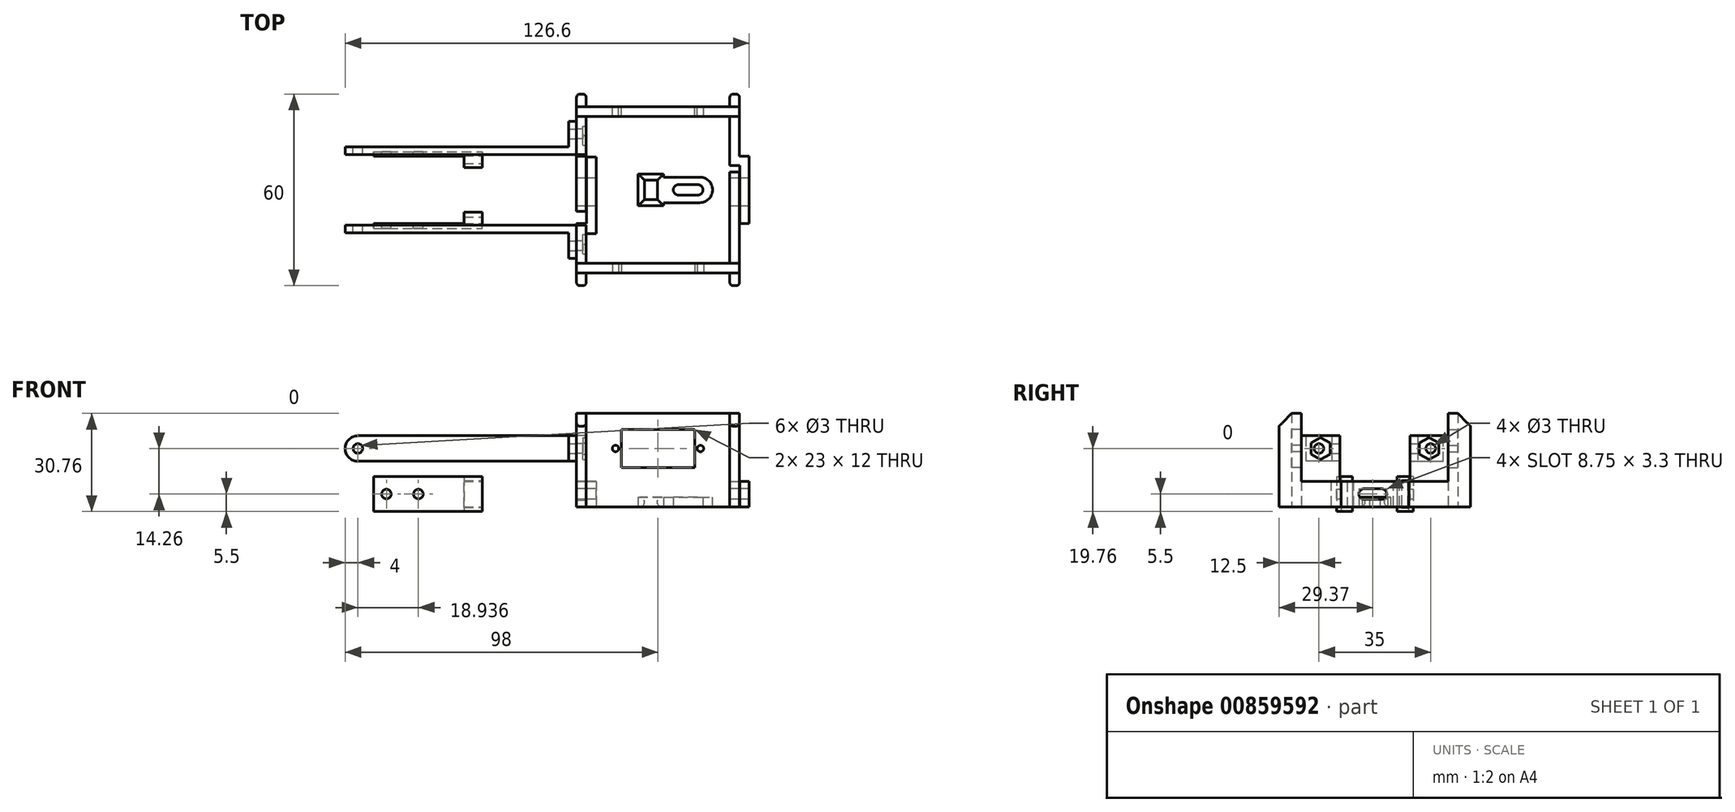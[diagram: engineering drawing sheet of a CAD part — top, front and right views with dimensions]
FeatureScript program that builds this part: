
annotation { "Feature Type Name" : "Feature", "Feature Type Description" : "" }
export const myFeature = defineFeature(function(context is Context, id is Id, definition is map)
    precondition{}
    {
        {
            var Q0;
            Q0=qCreatedBy(makeId("Top.planeOp"),FACE);
            var sketch = newSketch(context, id + "F0", { "sketchPlane" : qUnion([Q0])});
            skLineSegment(sketch, "E0", {"start": v(-48.06, 0) * mm, "end": v(-48.06, 8.5) * mm, "construction": true});
            skLineSegment(sketch, "E1", {"start": v(-48.06, 8.5) * mm, "end": v(-73.06, 8.5) * mm, "construction": true});
            skLineSegment(sketch, "E2", {"start": v(-73.06, 8.5) * mm, "end": v(-73.06, 10.5) * mm, "construction": true});
            skLineSegment(sketch, "E3.MirrorCS", {"start": v(-73.06, -8.5) * mm, "end": v(-73.06, -10.5) * mm, "construction": true});
            skLineSegment(sketch, "E4.MirrorCS", {"start": v(-48.06, -8.5) * mm, "end": v(-73.06, -8.5) * mm, "construction": true});
            skLineSegment(sketch, "E5.MirrorCS", {"start": v(-48.06, 0) * mm, "end": v(-48.06, -8.5) * mm, "construction": true});
            skLineSegment(sketch, "E6.bottom", {"start": v(-22.5, -23) * mm, "end": v(22.5, -23) * mm});
            skLineSegment(sketch, "E6.top", {"start": v(-22.5, 23) * mm, "end": v(22.5, 23) * mm});
            skLineSegment(sketch, "E6.left", {"start": v(-22.5, -23) * mm, "end": v(-22.5, -10.5) * mm});
            skLineSegment(sketch, "E6.right", {"start": v(22.5, -23) * mm, "end": v(22.5, -10.5) * mm});
            skPoint(sketch, "E6.middle", {"position": v(0, 0) * mm});
            skLineSegment(sketch, "E7", {"start": v(-73.06, 10.5) * mm, "end": v(-25.5, 10.5) * mm, "construction": true});
            skLineSegment(sketch, "E8", {"start": v(-25.5, 10.5) * mm, "end": v(-25.5, 26) * mm});
            skLineSegment(sketch, "E9", {"start": v(-25.5, 26) * mm, "end": v(25.5, 26) * mm});
            skLineSegment(sketch, "E10", {"start": v(25.5, 26) * mm, "end": v(25.5, 10.5) * mm});
            skLineSegment(sketch, "E11.MirrorCS", {"start": v(-73.06, -10.5) * mm, "end": v(-25.5, -10.5) * mm, "construction": true});
            skLineSegment(sketch, "E12.MirrorCS", {"start": v(-25.5, -10.5) * mm, "end": v(-25.5, -26) * mm});
            skLineSegment(sketch, "E13.MirrorCS", {"start": v(-25.5, -26) * mm, "end": v(25.5, -26) * mm});
            skLineSegment(sketch, "E14.MirrorCS", {"start": v(25.5, -26) * mm, "end": v(25.5, -10.5) * mm});
            skLineSegment(sketch, "E15", {"start": v(-25.5, 10.5) * mm, "end": v(-25.5, -10.5) * mm, "construction": true});
            skLineSegment(sketch, "E16", {"start": v(-25.5, -10.5) * mm, "end": v(-22.5, -10.5) * mm});
            skLineSegment(sketch, "E17", {"start": v(22.5, -10.5) * mm, "end": v(25.5, -10.5) * mm});
            skLineSegment(sketch, "E18", {"start": v(-25.5, 10.5) * mm, "end": v(-22.5, 10.5) * mm});
            skLineSegment(sketch, "E19", {"start": v(22.5, 10.5) * mm, "end": v(25.5, 10.5) * mm});
            skLineSegment(sketch, "E20.trimOffspring", {"start": v(22.5, 10.5) * mm, "end": v(22.5, 23) * mm});
            skPoint(sketch, "E21.orphan", {"position": v(25.5, 0) * mm});
            skLineSegment(sketch, "E22.trimOffspring", {"start": v(-22.5, 10.5) * mm, "end": v(-22.5, 23) * mm});
            skSolve(sketch);
        }
        {
            var Q0;
            Q0 = qSketchRegion(id + "F0", true);
            extrude(context, id + "F1", {"entities" : qUnion([Q0]), "depth" : 8 * mm, "offsetDistance" : 25 * mm});
        }
        {
            var Q0;
            Q0=makeQuery(id+"F1.opExtrude","SWEPT_FACE",FACE,{"disambiguationData":[OSD([sQuery(id+"F0.wireOp",EDGE,"E13.MirrorCS")])]});
            var sketch = newSketch(context, id + "F2", { "sketchPlane" : qUnion([Q0])});
            skLineSegment(sketch, "E23.bottom", {"start": v(11.5, 12.26) * mm, "end": v(-11.5, 12.26) * mm});
            skLineSegment(sketch, "E23.top", {"start": v(11.5, 24.26) * mm, "end": v(-11.5, 24.26) * mm});
            skLineSegment(sketch, "E23.left", {"start": v(11.5, 12.26) * mm, "end": v(11.5, 24.26) * mm});
            skLineSegment(sketch, "E23.right", {"start": v(-11.5, 12.26) * mm, "end": v(-11.5, 24.26) * mm});
            skLineSegment(sketch, "E24.bottom", {"start": v(25.5, 8) * mm, "end": v(0, 8) * mm});
            skLineSegment(sketch, "E24.top", {"start": v(25.5, 29.26) * mm, "end": v(-25.5, 29.26) * mm});
            skLineSegment(sketch, "E24.left", {"start": v(25.5, 8) * mm, "end": v(25.5, 29.26) * mm});
            skLineSegment(sketch, "E24.right", {"start": v(-25.5, 8) * mm, "end": v(-25.5, 29.26) * mm});
            skCircle(sketch, "E25", {"center": v(13.3, 18.26) * mm, "radius": 1 * mm});
            skPoint(sketch, "E25.centerSnap0", {"position": v(11.5, 18.26) * mm});
            skCircle(sketch, "E26", {"center": v(-13.3, 18.26) * mm, "radius": 1 * mm});
            skPoint(sketch, "E26.centerSnap0", {"position": v(-11.5, 18.26) * mm});
            skLineSegment(sketch, "E27", {"start": v(0, 12.26) * mm, "end": v(0, 24.26) * mm, "construction": true});
            skLineSegment(sketch, "E28.MirrorCS", {"start": v(-76.5, 8) * mm, "end": v(-51, 8) * mm});
            skLineSegment(sketch, "E29.MirrorCS", {"start": v(22.06, 8) * mm, "end": v(-76.5, 8) * mm, "construction": true});
            skPoint(sketch, "E30.MirrorCS.end.orphan", {"position": v(-25.5, 29.26) * mm});
            skPoint(sketch, "E30.MirrorCS.start.orphan", {"position": v(-76.5, 29.26) * mm});
            skLineSegment(sketch, "E31.trimOffspring", {"start": v(-25.5, 8) * mm, "end": v(25.5, 8) * mm});
            skSolve(sketch);
        }
        {
            var Q0;
            Q0=makeQuery(id+"F2.imprint","IMPRINT",FACE,{"disambiguationData":[TD([[makeQuery(id+"F2.imprint","IMPRINT",EDGE,{"derivedFrom":sQuery(id+"F2.wireOp",EDGE,"E23.bottom")}),1.0]])]});
            var Q1;
            {var subQ1=sQuery(id+"F2.wireOp",EDGE,"E24.right");Q1=makeQuery(id+"F2.imprint","IMPRINT",FACE,{"disambiguationData":[TD([[makeQuery(id+"F2.imprint","IMPRINT",EDGE,{"derivedFrom":subQ1}),1.0]])]});}
            var Q2;
            Q2=makeQuery(id+"F1.opExtrude","SWEPT_FACE",FACE,{"disambiguationData":[OSD([sQuery(id+"F0.wireOp",EDGE,"E6.bottom")])]});
            extrude(context, id + "F3", {"entities" : qUnion([Q0, Q1]), "operationType" : NewBodyOperationType.ADD, "endBound" : BoundingType.UP_TO_SURFACE, "oppositeDirection" : true, "depth" : 25 * mm, "endBoundEntityFace" : qUnion([Q2]), "offsetDistance" : 25 * mm});
        }
        {
            var Q0;
            Q0=makeQuery(id+"F3.boolean.opBoolean","MERGE",FACE,{"derivedFrom":[makeQuery(id+"F1.opExtrude","SWEPT_FACE",FACE,{"disambiguationData":[OSD([sQuery(id+"F0.wireOp",EDGE,"28178227-cdee-4869-aa74-51b11bafd0843.MirrorCS"),sQuery(id+"F0.wireOp",EDGE,"28178227-cdee-4869-aa74-51b11bafd0844.MirrorCS")])]}),makeQuery(id+"F3.opExtrude","CAP_FACE",FACE,{"disambiguationData":[OSD([sQuery(id+"F2.wireOp",EDGE,"E23.bottom"),sQuery(id+"F2.wireOp",EDGE,"E23.top"),sQuery(id+"F2.wireOp",EDGE,"E23.left"),sQuery(id+"F2.wireOp",EDGE,"E23.right"),sQuery(id+"F2.wireOp",EDGE,"E24.bottom"),sQuery(id+"F2.wireOp",EDGE,"E24.top"),sQuery(id+"F2.wireOp",EDGE,"E24.left"),sQuery(id+"F2.wireOp",EDGE,"E24.right"),sQuery(id+"F2.wireOp",EDGE,"E25"),sQuery(id+"F2.wireOp",EDGE,"E26")])],"isStart":true})]});
            var sketch = newSketch(context, id + "F4", { "sketchPlane" : qUnion([Q0])});
            skLineSegment(sketch, "E32", {"start": v(0, 29.26) * mm, "end": v(0, 3.18) * mm, "construction": true});
            skLineSegment(sketch, "E33.bottom", {"start": v(-25.5, 29.26) * mm, "end": v(-22.5, 29.26) * mm});
            skLineSegment(sketch, "E33.top", {"start": v(-25.5, 0) * mm, "end": v(-22.5, 0) * mm});
            skLineSegment(sketch, "E33.left", {"start": v(-25.5, 29.26) * mm, "end": v(-25.5, 0) * mm});
            skLineSegment(sketch, "E33.right", {"start": v(-22.5, 29.26) * mm, "end": v(-22.5, 0) * mm});
            skLineSegment(sketch, "E34.MirrorCS", {"start": v(25.5, 29.26) * mm, "end": v(22.5, 29.26) * mm});
            skLineSegment(sketch, "E35.MirrorCS", {"start": v(25.5, 0) * mm, "end": v(22.5, 0) * mm});
            skLineSegment(sketch, "E36.MirrorCS", {"start": v(25.5, 29.26) * mm, "end": v(25.5, 0) * mm});
            skLineSegment(sketch, "E37.MirrorCS", {"start": v(22.5, 29.26) * mm, "end": v(22.5, 0) * mm});
            skSolve(sketch);
        }
        {
            var Q0;
            Q0 = qSketchRegion(id + "F4", true);
            extrude(context, id + "F5", {"entities" : qUnion([Q0]), "operationType" : NewBodyOperationType.ADD, "depth" : 4 * mm, "offsetDistance" : 25 * mm});
        }
        {
            var Q0;
            Q0=makeQuery(id+"F11.boolean.opBoolean","MERGE",FACE,{"derivedFrom":[makeQuery(id+"F1.opExtrude","SWEPT_FACE",FACE,{"disambiguationData":[OSD([sQuery(id+"F0.wireOp",EDGE,"E9")])]}),makeQuery(id+"F11.opExtrude","CAP_FACE",FACE,{"disambiguationData":[OSD([sQuery(id+"F10.wireOp",EDGE,"E46.0"),sQuery(id+"F10.wireOp",EDGE,"E48.0"),sQuery(id+"F10.wireOp",EDGE,"E49.0"),sQuery(id+"F10.wireOp",EDGE,"E50.0"),sQuery(id+"F10.wireOp",EDGE,"E51.0"),sQuery(id+"F10.wireOp",EDGE,"E52.0"),sQuery(id+"F10.wireOp",EDGE,"E53.0"),sQuery(id+"F10.wireOp",EDGE,"E54.0"),sQuery(id+"F10.wireOp",EDGE,"E55.0"),sQuery(id+"F10.wireOp",EDGE,"E56")])],"isStart":true})]});
            var sketch = newSketch(context, id + "F6", { "sketchPlane" : qUnion([Q0])});
            skLineSegment(sketch, "E38.0", {"start": v(22.5, 29.26) * mm, "end": v(22.5, 0) * mm});
            skLineSegment(sketch, "E39.0", {"start": v(-22.5, 29.26) * mm, "end": v(-22.5, 0) * mm});
            skLineSegment(sketch, "E40.0", {"start": v(25.5, 29.26) * mm, "end": v(25.5, 0) * mm});
            skLineSegment(sketch, "E41.0", {"start": v(-25.5, 29.26) * mm, "end": v(-25.5, 0) * mm});
            skLineSegment(sketch, "E42", {"start": v(-25.5, 29.26) * mm, "end": v(-22.5, 29.26) * mm});
            skLineSegment(sketch, "E43", {"start": v(-25.5, 0) * mm, "end": v(-22.5, 0) * mm});
            skLineSegment(sketch, "E44", {"start": v(22.5, 0) * mm, "end": v(25.5, 0) * mm});
            skLineSegment(sketch, "E45", {"start": v(22.5, 29.26) * mm, "end": v(25.5, 29.26) * mm});
            skSolve(sketch);
        }
        {
            var Q0;
            Q0 = qSketchRegion(id + "F6", true);
            extrude(context, id + "F7", {"entities" : qUnion([Q0]), "operationType" : NewBodyOperationType.ADD, "depth" : 4 * mm, "offsetDistance" : 25 * mm});
        }
        {
            var Q0;
            Q0=makeQuery(id+"F5.opExtrude","CAP_EDGE",EDGE,{"disambiguationData":[OSD([sQuery(id+"F4.wireOp",EDGE,"E33.bottom")])],"isStart":false});
            var Q1;
            Q1=makeQuery(id+"F5.opExtrude","CAP_EDGE",EDGE,{"disambiguationData":[OSD([sQuery(id+"F4.wireOp",EDGE,"E34.MirrorCS")])],"isStart":false});
            var Q2;
            Q2=makeQuery(id+"F7.opExtrude","CAP_EDGE",EDGE,{"disambiguationData":[OSD([sQuery(id+"F6.wireOp",EDGE,"E42")])],"isStart":false});
            var Q3;
            Q3=makeQuery(id+"F7.opExtrude","CAP_EDGE",EDGE,{"disambiguationData":[OSD([sQuery(id+"F6.wireOp",EDGE,"E45")])],"isStart":false});
            chamfer(context, id + "F8", {"entities" : qUnion([Q0, Q1, Q2, Q3]), "width" : 4 * mm, "tangentPropagation" : true});
        }
        {
            var Q0;
            Q0=makeQuery(id+"F5.opExtrude","CAP_EDGE",EDGE,{"disambiguationData":[OSD([sQuery(id+"F4.wireOp",EDGE,"E33.left")])],"isStart":false});
            var Q1;
            Q1=makeQuery(id+"F5.opExtrude","CAP_EDGE",EDGE,{"disambiguationData":[OSD([sQuery(id+"F4.wireOp",EDGE,"E33.right")])],"isStart":false});
            var Q2;
            Q2=makeQuery(id+"F5.opExtrude","CAP_EDGE",EDGE,{"disambiguationData":[OSD([sQuery(id+"F4.wireOp",EDGE,"E37.MirrorCS")])],"isStart":false});
            var Q3;
            Q3=makeQuery(id+"F5.opExtrude","CAP_EDGE",EDGE,{"disambiguationData":[OSD([sQuery(id+"F4.wireOp",EDGE,"E36.MirrorCS")])],"isStart":false});
            var Q4;
            Q4=makeQuery(id+"F7.opExtrude","CAP_EDGE",EDGE,{"disambiguationData":[OSD([sQuery(id+"F6.wireOp",EDGE,"E41.0")])],"isStart":false});
            var Q5;
            Q5=makeQuery(id+"F7.opExtrude","CAP_EDGE",EDGE,{"disambiguationData":[OSD([sQuery(id+"F6.wireOp",EDGE,"E39.0")])],"isStart":false});
            var Q6;
            Q6=makeQuery(id+"F7.opExtrude","CAP_EDGE",EDGE,{"disambiguationData":[OSD([sQuery(id+"F6.wireOp",EDGE,"E38.0")])],"isStart":false});
            var Q7;
            Q7=makeQuery(id+"F7.opExtrude","CAP_EDGE",EDGE,{"disambiguationData":[OSD([sQuery(id+"F6.wireOp",EDGE,"E40.0")])],"isStart":false});
            fillet(context, id + "F9", {"entities" : qUnion([Q0, Q1, Q2, Q3, Q4, Q5, Q6, Q7]), "radius" : 1 * mm, "tangentPropagation" : true, "allowEdgeOverflow" : false});
        }
        {
            var Q0;
            Q0=makeQuery(id+"F1.opExtrude","SWEPT_FACE",FACE,{"disambiguationData":[OSD([sQuery(id+"F0.wireOp",EDGE,"E9")])]});
            var sketch = newSketch(context, id + "F10", { "sketchPlane" : qUnion([Q0])});
            skLineSegment(sketch, "E46.0", {"start": v(-25.5, 8) * mm, "end": v(-25.5, 29.26) * mm});
            skLineSegment(sketch, "E47.0", {"start": v(-22.5, 29.26) * mm, "end": v(22.5, 29.26) * mm});
            skLineSegment(sketch, "E48.0", {"start": v(-25.5, 29.26) * mm, "end": v(25.5, 29.26) * mm});
            skLineSegment(sketch, "E49.0", {"start": v(25.5, 8) * mm, "end": v(25.5, 29.26) * mm});
            skLineSegment(sketch, "E50.0", {"start": v(-11.5, 24.26) * mm, "end": v(11.5, 24.26) * mm});
            skLineSegment(sketch, "E51.0", {"start": v(11.5, 12.26) * mm, "end": v(11.5, 24.26) * mm});
            skLineSegment(sketch, "E52.0", {"start": v(-11.5, 12.26) * mm, "end": v(-11.5, 24.26) * mm});
            skLineSegment(sketch, "E53.0", {"start": v(-11.5, 12.26) * mm, "end": v(11.5, 12.26) * mm});
            skCircle(sketch, "E54.0", {"center": v(-13.3, 18.26) * mm, "radius": 1 * mm});
            skCircle(sketch, "E55.0", {"center": v(13.3, 18.26) * mm, "radius": 1 * mm});
            skLineSegment(sketch, "E56", {"start": v(-25.5, 8) * mm, "end": v(25.5, 8) * mm});
            skSolve(sketch);
        }
        {
            var Q0;
            {var subQ2=sQuery(id+"F10.wireOp",EDGE,"E46.0");Q0=makeQuery(id+"F10.imprint","IMPRINT",FACE,{"disambiguationData":[TD([[makeQuery(id+"F10.imprint","IMPRINT",EDGE,{"derivedFrom":subQ2}),-1.0]])]});}
            var Q1;
            Q1=makeQuery(id+"F1.opExtrude","SWEPT_FACE",FACE,{"disambiguationData":[OSD([sQuery(id+"F0.wireOp",EDGE,"E6.top")])]});
            extrude(context, id + "F11", {"entities" : qUnion([Q0]), "operationType" : NewBodyOperationType.ADD, "endBound" : BoundingType.UP_TO_SURFACE, "oppositeDirection" : true, "depth" : 25 * mm, "endBoundEntityFace" : qUnion([Q1]), "offsetDistance" : 25 * mm});
        }
        {
            var Q0;
            Q0=qCreatedBy(makeId("Right.planeOp"),FACE);
            cPlane(context, id + "F12", {"entities" : qUnion([Q0]), "cplaneType" : CPlaneType.OFFSET, "offset" : 55 * mm, "oppositeDirection" : true, "width" : 150 * mm, "height" : 150 * mm});
        }
        {
            var Q0;
            Q0=qCreatedBy(id+"F12.planeOp",FACE);
            var sketch = newSketch(context, id + "F13", { "sketchPlane" : qUnion([Q0])});
            skLineSegment(sketch, "E57.0", {"start": v(8.5, 0) * mm, "end": v(8.5, 8) * mm});
            skLineSegment(sketch, "E58.0", {"start": v(10.5, 8) * mm, "end": v(10.5, 0) * mm});
            skLineSegment(sketch, "E59.0.0", {"start": v(-10.5, 8) * mm, "end": v(-8.5, 8) * mm});
            skLineSegment(sketch, "E59.0.1", {"start": v(-8.5, 0) * mm, "end": v(-8.5, 8) * mm});
            skLineSegment(sketch, "E59.0.2", {"start": v(-10.5, 0) * mm, "end": v(-8.5, 0) * mm});
            skLineSegment(sketch, "E59.0.3", {"start": v(-10.5, 8) * mm, "end": v(-10.5, 0) * mm});
            skLineSegment(sketch, "E60.0.0", {"start": v(10.5, 0) * mm, "end": v(10.5, 8) * mm});
            skLineSegment(sketch, "E60.0.1", {"start": v(10.5, 0) * mm, "end": v(8.5, 0) * mm});
            skLineSegment(sketch, "E60.0.2", {"start": v(8.5, 8) * mm, "end": v(8.5, 0) * mm});
            skLineSegment(sketch, "E60.0.3", {"start": v(10.5, 8) * mm, "end": v(8.5, 8) * mm});
            skLineSegment(sketch, "E61.bottom", {"start": v(12, 9.5) * mm, "end": v(7, 9.5) * mm});
            skLineSegment(sketch, "E61.top", {"start": v(12, -1.5) * mm, "end": v(7, -1.5) * mm});
            skLineSegment(sketch, "E61.left", {"start": v(12, 9.5) * mm, "end": v(12, -1.5) * mm});
            skLineSegment(sketch, "E61.right", {"start": v(7, 9.5) * mm, "end": v(7, -1.5) * mm});
            skLineSegment(sketch, "E62.MirrorCS", {"start": v(-12, 9.5) * mm, "end": v(-7, 9.5) * mm});
            skLineSegment(sketch, "E63.MirrorCS", {"start": v(-7, 9.5) * mm, "end": v(-7, -1.5) * mm});
            skLineSegment(sketch, "E64.MirrorCS", {"start": v(-8.5, 8) * mm, "end": v(-8.5, 0) * mm});
            skLineSegment(sketch, "E65.MirrorCS", {"start": v(-12, -1.5) * mm, "end": v(-7, -1.5) * mm});
            skLineSegment(sketch, "E66.MirrorCS", {"start": v(-10.5, 0) * mm, "end": v(-10.5, 8) * mm});
            skLineSegment(sketch, "E67.MirrorCS", {"start": v(-12, 9.5) * mm, "end": v(-12, -1.5) * mm});
            skLineSegment(sketch, "E68.0", {"start": v(10.7, 8.2) * mm, "end": v(8.3, 8.2) * mm});
            skLineSegment(sketch, "E68.1", {"start": v(10.7, -0.2) * mm, "end": v(10.7, 8.2) * mm});
            skLineSegment(sketch, "E68.2", {"start": v(10.7, -0.2) * mm, "end": v(8.3, -0.2) * mm});
            skLineSegment(sketch, "E68.3", {"start": v(8.3, 8.2) * mm, "end": v(8.3, -0.2) * mm});
            skSolve(sketch);
        }
        {
            var Q0;
            Q0 = qSketchRegion(id + "F13", true);
            extrude(context, id + "F14", {"entities" : qUnion([Q0]), "oppositeDirection" : true, "depth" : 5.8 * mm, "offsetDistance" : 25 * mm});
        }
        {
            var Q0;
            Q0=makeQuery(id+"F14.opExtrude","SWEPT_FACE",FACE,{"disambiguationData":[OSD([sQuery(id+"F13.wireOp",EDGE,"E61.top")])]});
            var sketch = newSketch(context, id + "F15", { "sketchPlane" : qUnion([Q0])});
            skLineSegment(sketch, "E69", {"start": v(-60.8, -7) * mm, "end": v(-60.8, -7) * mm});
            skLineSegment(sketch, "E70", {"start": v(-60.8, -7) * mm, "end": v(-60.8, -10.5) * mm});
            skLineSegment(sketch, "E71", {"start": v(-60.8, -10.5) * mm, "end": v(-89.06, -10.5) * mm});
            skLineSegment(sketch, "E72", {"start": v(-89.06, -10.5) * mm, "end": v(-89.06, -12) * mm});
            skLineSegment(sketch, "E73", {"start": v(-89.06, -12) * mm, "end": v(-60.8, -12) * mm});
            skLineSegment(sketch, "E74", {"start": v(-60.8, -12) * mm, "end": v(-60.8, -7) * mm});
            skLineSegment(sketch, "E75.MirrorCS", {"start": v(-60.8, 7) * mm, "end": v(-60.8, 7) * mm});
            skLineSegment(sketch, "E76.MirrorCS", {"start": v(-89.06, 10.5) * mm, "end": v(-89.06, 12) * mm});
            skLineSegment(sketch, "E77.MirrorCS", {"start": v(-89.06, 12) * mm, "end": v(-60.8, 12) * mm});
            skLineSegment(sketch, "E78.MirrorCS", {"start": v(-60.8, 10.5) * mm, "end": v(-89.06, 10.5) * mm});
            skLineSegment(sketch, "E79.MirrorCS", {"start": v(-60.8, 7) * mm, "end": v(-60.8, 10.5) * mm});
            skLineSegment(sketch, "E80.MirrorCS", {"start": v(-60.8, 12) * mm, "end": v(-60.8, 7) * mm});
            skLineSegment(sketch, "E81", {"start": v(-73.06, -10.5) * mm, "end": v(-73.06, -8.5) * mm, "construction": true});
            skSolve(sketch);
        }
        {
            var Q0;
            Q0 = qSketchRegion(id + "F15", true);
            var Q1;
            Q1=makeQuery(id+"F14.opExtrude","SWEPT_FACE",FACE,{"disambiguationData":[OSD([sQuery(id+"F13.wireOp",EDGE,"E62.MirrorCS")])]});
            extrude(context, id + "F16", {"entities" : qUnion([Q0]), "operationType" : NewBodyOperationType.ADD, "endBound" : BoundingType.UP_TO_SURFACE, "oppositeDirection" : true, "depth" : 25 * mm, "endBoundEntityFace" : qUnion([Q1]), "offsetDistance" : 25 * mm});
        }
        {
            var Q0;
            Q0=makeQuery(id+"F16.boolean.opBoolean","MERGE",FACE,{"derivedFrom":[makeQuery(id+"F14.opExtrude","SWEPT_FACE",FACE,{"disambiguationData":[OSD([sQuery(id+"F13.wireOp",EDGE,"E61.left")])]}),makeQuery(id+"F16.opExtrude","SWEPT_FACE",FACE,{"disambiguationData":[OSD([sQuery(id+"F15.wireOp",EDGE,"E73")])]})]});
            var sketch = newSketch(context, id + "F17", { "sketchPlane" : qUnion([Q0])});
            skCircle(sketch, "E82.0", {"center": v(75.06, 4) * mm, "radius": 1.5 * mm});
            skCircle(sketch, "E83", {"center": v(85.06, 4) * mm, "radius": 1.5 * mm});
            skSolve(sketch);
        }
        {
            var Q0;
            Q0 = qSketchRegion(id + "F17", true);
            var Q1;
            Q1=makeQuery(id+"F16.boolean.opBoolean","MERGE",FACE,{"derivedFrom":[makeQuery(id+"F14.opExtrude","SWEPT_FACE",FACE,{"disambiguationData":[OSD([sQuery(id+"F13.wireOp",EDGE,"E67.MirrorCS")])]}),makeQuery(id+"F16.opExtrude","SWEPT_FACE",FACE,{"disambiguationData":[OSD([sQuery(id+"F15.wireOp",EDGE,"E77.MirrorCS")])]})]});
            extrude(context, id + "F18", {"entities" : qUnion([Q0]), "operationType" : NewBodyOperationType.REMOVE, "endBound" : BoundingType.UP_TO_SURFACE, "oppositeDirection" : true, "depth" : 25 * mm, "endBoundEntityFace" : qUnion([Q1]), "offsetDistance" : 25 * mm});
        }
        {
            var Q0;
            Q0=makeQuery(id+"F11.boolean.opBoolean","MERGE",FACE,{"derivedFrom":[makeQuery(id+"F7.boolean.opBoolean","MERGE",FACE,{"derivedFrom":[makeQuery(id+"F5.boolean.opBoolean","MERGE",FACE,{"derivedFrom":[makeQuery(id+"F3.boolean.opBoolean","MERGE",FACE,{"derivedFrom":[makeQuery(id+"F1.opExtrude","SWEPT_FACE",FACE,{"disambiguationData":[OSD([sQuery(id+"F0.wireOp",EDGE,"E8"),sQuery(id+"F0.wireOp",EDGE,"E12.MirrorCS"),sQuery(id+"F0.wireOp",EDGE,"E15")])]}),makeQuery(id+"F3.opExtrude","SWEPT_FACE",FACE,{"disambiguationData":[OSD([sQuery(id+"F2.wireOp",EDGE,"E24.right")])]})]}),makeQuery(id+"F5.opExtrude","SWEPT_FACE",FACE,{"disambiguationData":[OSD([sQuery(id+"F4.wireOp",EDGE,"E33.left")])]})]}),makeQuery(id+"F7.opExtrude","SWEPT_FACE",FACE,{"disambiguationData":[OSD([sQuery(id+"F6.wireOp",EDGE,"E40.0")])]})]}),makeQuery(id+"F11.opExtrude","SWEPT_FACE",FACE,{"disambiguationData":[OSD([sQuery(id+"F10.wireOp",EDGE,"E49.0")])]})]});
            var sketch = newSketch(context, id + "F19", { "sketchPlane" : qUnion([Q0])});
            skLineSegment(sketch, "E84.0", {"start": v(-23, 8) * mm, "end": v(23, 8) * mm});
            skLineSegment(sketch, "E85.0", {"start": v(-23, 29.26) * mm, "end": v(-23, 8) * mm});
            skLineSegment(sketch, "E86.0", {"start": v(23, 8) * mm, "end": v(23, 29.26) * mm});
            skLineSegment(sketch, "E87.0", {"start": v(23, 19.26) * mm, "end": v(23, 17.26) * mm});
            skLineSegment(sketch, "E88", {"start": v(23, 22.26) * mm, "end": v(11, 22.26) * mm});
            skLineSegment(sketch, "E89", {"start": v(11, 22.26) * mm, "end": v(11, 8) * mm});
            skCircle(sketch, "E90", {"center": v(17.5, 18.26) * mm, "radius": 1.5 * mm});
            skPoint(sketch, "E90.centerSnap0", {"position": v(23, 18.26) * mm});
            skLineSegment(sketch, "E91.MirrorCS", {"start": v(-23, 22.26) * mm, "end": v(-11, 22.26) * mm});
            skLineSegment(sketch, "E92.MirrorCS", {"start": v(-11, 22.26) * mm, "end": v(-11, 8) * mm});
            skCircle(sketch, "E93.MirrorC", {"center": v(-17.5, 18.26) * mm, "radius": 1.5 * mm});
            skSolve(sketch);
        }
        {
            var Q0;
            Q0 = qSketchRegion(id + "F19", true);
            var Q1;
            Q1=makeQuery(id+"F1.opExtrude","SWEPT_FACE",FACE,{"disambiguationData":[OSD([sQuery(id+"F0.wireOp",EDGE,"E6.left")])]});
            extrude(context, id + "F20", {"entities" : qUnion([Q0]), "operationType" : NewBodyOperationType.ADD, "endBound" : BoundingType.UP_TO_SURFACE, "oppositeDirection" : true, "depth" : 25 * mm, "endBoundEntityFace" : qUnion([Q1]), "offsetDistance" : 25 * mm});
        }
        {
            var Q0;
            Q0=makeQuery(id+"F1.opExtrude","SWEPT_FACE",FACE,{"disambiguationData":[OSD([sQuery(id+"F0.wireOp",EDGE,"E8"),sQuery(id+"F0.wireOp",EDGE,"E12.MirrorCS"),sQuery(id+"F0.wireOp",EDGE,"E15")])]});
            var sketch = newSketch(context, id + "F21", { "sketchPlane" : qUnion([Q0])});
            skLineSegment(sketch, "E94.0", {"start": v(9.37, 8) * mm, "end": v(-11, 8) * mm});
            skLineSegment(sketch, "E95.0", {"start": v(9.37, 8) * mm, "end": v(9.37, 0) * mm});
            skLineSegment(sketch, "E96.0", {"start": v(-11, 8) * mm, "end": v(-11, 0) * mm});
            skLineSegment(sketch, "E97", {"start": v(9.37, 2) * mm, "end": v(-11, 2) * mm});
            skLineSegment(sketch, "E98.0", {"start": v(4, 0) * mm, "end": v(-11, 0) * mm, "construction": true});
            skSolve(sketch);
        }
        {
            var Q0;
            Q0 = qSketchRegion(id + "F21", true);
            var Q1;
            Q1=makeQuery(id+"F1.opExtrude","SWEPT_FACE",FACE,{"disambiguationData":[OSD([sQuery(id+"F0.wireOp",EDGE,"E6.right")])]});
            extrude(context, id + "F22", {"entities" : qUnion([Q0]), "operationType" : NewBodyOperationType.REMOVE, "endBound" : BoundingType.UP_TO_SURFACE, "oppositeDirection" : true, "depth" : 25 * mm, "endBoundEntityFace" : qUnion([Q1]), "offsetDistance" : 25 * mm});
        }
        {
            var Q0;
            {var subQ0=sQuery(id+"F19.wireOp",EDGE,"E84.0");Q0=makeQuery(id+"F20.boolean.opBoolean","MERGE",FACE,{"derivedFrom":[makeQuery(id+"F11.boolean.opBoolean","MERGE",FACE,{"derivedFrom":[makeQuery(id+"F7.boolean.opBoolean","MERGE",FACE,{"derivedFrom":[makeQuery(id+"F5.boolean.opBoolean","MERGE",FACE,{"derivedFrom":[makeQuery(id+"F3.boolean.opBoolean","MERGE",FACE,{"derivedFrom":[makeQuery(id+"F1.opExtrude","SWEPT_FACE",FACE,{"disambiguationData":[OSD([sQuery(id+"F0.wireOp",EDGE,"E8"),sQuery(id+"F0.wireOp",EDGE,"E12.MirrorCS"),sQuery(id+"F0.wireOp",EDGE,"E15")])]}),makeQuery(id+"F3.opExtrude","SWEPT_FACE",FACE,{"disambiguationData":[OSD([sQuery(id+"F2.wireOp",EDGE,"E24.right")])]})]}),makeQuery(id+"F5.opExtrude","SWEPT_FACE",FACE,{"disambiguationData":[OSD([sQuery(id+"F4.wireOp",EDGE,"E33.left")])]})]}),makeQuery(id+"F7.opExtrude","SWEPT_FACE",FACE,{"disambiguationData":[OSD([sQuery(id+"F6.wireOp",EDGE,"E40.0")])]})]}),makeQuery(id+"F11.opExtrude","SWEPT_FACE",FACE,{"disambiguationData":[OSD([sQuery(id+"F10.wireOp",EDGE,"E49.0")])]})]}),makeQuery(id+"F20.opExtrude","CAP_FACE",FACE,{"disambiguationData":[OSD([subQ0,sQuery(id+"F19.wireOp",EDGE,"E85.0"),sQuery(id+"F19.wireOp",EDGE,"E91.MirrorCS"),sQuery(id+"F19.wireOp",EDGE,"E92.MirrorCS"),sQuery(id+"F19.wireOp",EDGE,"E93.MirrorC")])],"isStart":true}),makeQuery(id+"F20.opExtrude","CAP_FACE",FACE,{"disambiguationData":[OSD([subQ0,sQuery(id+"F19.wireOp",EDGE,"E86.0"),sQuery(id+"F19.wireOp",EDGE,"E87.0"),sQuery(id+"F19.wireOp",EDGE,"E88"),sQuery(id+"F19.wireOp",EDGE,"E89"),sQuery(id+"F19.wireOp",EDGE,"E90")])],"isStart":true})]});}
            var sketch = newSketch(context, id + "F23", { "sketchPlane" : qUnion([Q0])});
            skLineSegment(sketch, "E99.0", {"start": v(-23, 22.26) * mm, "end": v(-11, 22.26) * mm});
            skLineSegment(sketch, "E100.0", {"start": v(-11, 22.26) * mm, "end": v(-11, 2) * mm});
            skCircle(sketch, "E101.0", {"center": v(-17.5, 18.26) * mm, "radius": 1.5 * mm});
            skLineSegment(sketch, "E102", {"start": v(-11, 14.26) * mm, "end": v(-21.5, 14.26) * mm});
            skLineSegment(sketch, "E103", {"start": v(-21.5, 14.26) * mm, "end": v(-21.5, 22.26) * mm});
            skLineSegment(sketch, "E104.MirrorCS", {"start": v(23, 22.26) * mm, "end": v(11, 22.26) * mm});
            skCircle(sketch, "E105.MirrorC", {"center": v(17.5, 18.26) * mm, "radius": 1.5 * mm});
            skLineSegment(sketch, "E106.MirrorCS", {"start": v(11, 14.26) * mm, "end": v(21.5, 14.26) * mm});
            skLineSegment(sketch, "E107.MirrorCS", {"start": v(11, 22.26) * mm, "end": v(11, 2) * mm});
            skLineSegment(sketch, "E108.MirrorCS", {"start": v(21.5, 14.26) * mm, "end": v(21.5, 22.26) * mm});
            skSolve(sketch);
        }
        {
            var Q0;
            Q0 = qSketchRegion(id + "F23", true);
            extrude(context, id + "F24", {"entities" : qUnion([Q0]), "depth" : 2.5 * mm, "offsetDistance" : 25 * mm});
        }
        {
            var Q0;
            Q0=makeQuery(id+"F24.opExtrude","CAP_FACE",FACE,{"disambiguationData":[OSD([sQuery(id+"F23.wireOp",EDGE,"E99.0"),sQuery(id+"F23.wireOp",EDGE,"E100.0"),sQuery(id+"F23.wireOp",EDGE,"E101.0"),sQuery(id+"F23.wireOp",EDGE,"E102"),sQuery(id+"F23.wireOp",EDGE,"E103")])],"isStart":false});
            var sketch = newSketch(context, id + "F25", { "sketchPlane" : qUnion([Q0])});
            skLineSegment(sketch, "E109.bottom", {"start": v(-11, 22.26) * mm, "end": v(-13.5, 22.26) * mm});
            skLineSegment(sketch, "E109.top", {"start": v(-11, 14.26) * mm, "end": v(-13.5, 14.26) * mm});
            skLineSegment(sketch, "E109.left", {"start": v(-11, 22.26) * mm, "end": v(-11, 14.26) * mm});
            skLineSegment(sketch, "E109.right", {"start": v(-13.5, 22.26) * mm, "end": v(-13.5, 14.26) * mm});
            skLineSegment(sketch, "E110.MirrorCS", {"start": v(11, 22.26) * mm, "end": v(13.5, 22.26) * mm});
            skLineSegment(sketch, "E111.MirrorCS", {"start": v(11, 14.26) * mm, "end": v(13.5, 14.26) * mm});
            skLineSegment(sketch, "E112.MirrorCS", {"start": v(11, 22.26) * mm, "end": v(11, 14.26) * mm});
            skLineSegment(sketch, "E113.MirrorCS", {"start": v(13.5, 22.26) * mm, "end": v(13.5, 14.26) * mm});
            skSolve(sketch);
        }
        {
            var Q0;
            Q0 = qSketchRegion(id + "F25", true);
            extrude(context, id + "F26", {"entities" : qUnion([Q0]), "operationType" : NewBodyOperationType.ADD, "depth" : 70 * mm, "offsetDistance" : 25 * mm});
        }
        {
            var Q0;
            Q0=makeQuery(id+"F26.opExtrude","SWEPT_FACE",FACE,{"disambiguationData":[OSD([sQuery(id+"F25.wireOp",EDGE,"E109.right")])]});
            var sketch = newSketch(context, id + "F27", { "sketchPlane" : qUnion([Q0])});
            skCircle(sketch, "E114", {"center": v(94, 18.26) * mm, "radius": 1.5 * mm});
            skPoint(sketch, "E114.centerSnap0", {"position": v(98, 18.26) * mm});
            skSolve(sketch);
        }
        {
            var Q0;
            Q0 = qSketchRegion(id + "F27", true);
            extrude(context, id + "F28", {"entities" : qUnion([Q0]), "operationType" : NewBodyOperationType.REMOVE, "endBound" : BoundingType.THROUGH_ALL, "oppositeDirection" : true, "depth" : 25 * mm, "offsetDistance" : 25 * mm});
        }
        {
            var Q0;
            Q0=makeQuery(id+"F26.opExtrude","CAP_EDGE",EDGE,{"disambiguationData":[OSD([sQuery(id+"F25.wireOp",EDGE,"E109.bottom")])],"isStart":false});
            var Q1;
            Q1=makeQuery(id+"F26.opExtrude","CAP_EDGE",EDGE,{"disambiguationData":[OSD([sQuery(id+"F25.wireOp",EDGE,"E109.top")])],"isStart":false});
            var Q2;
            Q2=makeQuery(id+"F26.opExtrude","CAP_EDGE",EDGE,{"disambiguationData":[OSD([sQuery(id+"F25.wireOp",EDGE,"E110.MirrorCS")])],"isStart":false});
            var Q3;
            Q3=makeQuery(id+"F26.opExtrude","CAP_EDGE",EDGE,{"disambiguationData":[OSD([sQuery(id+"F25.wireOp",EDGE,"E111.MirrorCS")])],"isStart":false});
            fillet(context, id + "F29", {"entities" : qUnion([Q0, Q1, Q2, Q3]), "radius" : 4 * mm, "tangentPropagation" : true, "allowEdgeOverflow" : false});
        }
        {
            var Q0;
            {var subQ0=sQuery(id+"F19.wireOp",EDGE,"E84.0");Q0=makeQuery(id+"F20.boolean.opBoolean","MERGE",FACE,{"derivedFrom":[makeQuery(id+"F1.opExtrude","SWEPT_FACE",FACE,{"disambiguationData":[OSD([sQuery(id+"F0.wireOp",EDGE,"E6.left")])]}),makeQuery(id+"F20.opExtrude","CAP_FACE",FACE,{"disambiguationData":[OSD([subQ0,sQuery(id+"F19.wireOp",EDGE,"E85.0"),sQuery(id+"F19.wireOp",EDGE,"E91.MirrorCS"),sQuery(id+"F19.wireOp",EDGE,"E92.MirrorCS"),sQuery(id+"F19.wireOp",EDGE,"E93.MirrorC")])],"isStart":false}),makeQuery(id+"F20.opExtrude","CAP_FACE",FACE,{"disambiguationData":[OSD([subQ0,sQuery(id+"F19.wireOp",EDGE,"E86.0"),sQuery(id+"F19.wireOp",EDGE,"E87.0"),sQuery(id+"F19.wireOp",EDGE,"E88"),sQuery(id+"F19.wireOp",EDGE,"E89"),sQuery(id+"F19.wireOp",EDGE,"E90")])],"isStart":false})]});}
            var sketch = newSketch(context, id + "F30", { "sketchPlane" : qUnion([Q0])});
            skCircle(sketch, "E115.cCircle", {"center": v(-17, 18.26) * mm, "radius": 3 * mm, "construction": true});
            skLineSegment(sketch, "E115.0", {"start": v(-14, 20) * mm, "end": v(-14, 16.53) * mm});
            skLineSegment(sketch, "E115.1", {"start": v(-14, 16.53) * mm, "end": v(-17, 14.8) * mm});
            skLineSegment(sketch, "E115.2", {"start": v(-17, 14.8) * mm, "end": v(-20, 16.53) * mm});
            skLineSegment(sketch, "E115.3", {"start": v(-20, 16.53) * mm, "end": v(-20, 20) * mm});
            skLineSegment(sketch, "E115.4", {"start": v(-20, 20) * mm, "end": v(-17, 21.72) * mm});
            skLineSegment(sketch, "E115.5", {"start": v(-17, 21.72) * mm, "end": v(-14, 20) * mm});
            skPoint(sketch, "E115.0.midPoint", {"position": v(-14, 18.26) * mm});
            skLineSegment(sketch, "E116.MirrorCS", {"start": v(14, 20) * mm, "end": v(14, 16.53) * mm});
            skLineSegment(sketch, "E117.MirrorCS", {"start": v(14, 16.53) * mm, "end": v(17, 14.8) * mm});
            skLineSegment(sketch, "E118.MirrorCS", {"start": v(20, 20) * mm, "end": v(17, 21.72) * mm});
            skPoint(sketch, "E119.MirrorP", {"position": v(14, 18.26) * mm});
            skLineSegment(sketch, "E120.MirrorCS", {"start": v(17, 14.8) * mm, "end": v(20, 16.53) * mm});
            skCircle(sketch, "E121.MirrorC", {"center": v(17, 18.26) * mm, "radius": 3 * mm, "construction": true});
            skLineSegment(sketch, "E122.MirrorCS", {"start": v(20, 16.53) * mm, "end": v(20, 20) * mm});
            skLineSegment(sketch, "E123.MirrorCS", {"start": v(17, 21.72) * mm, "end": v(14, 20) * mm});
            skSolve(sketch);
        }
        {
            var Q0;
            Q0 = qSketchRegion(id + "F30", true);
            extrude(context, id + "F31", {"entities" : qUnion([Q0]), "operationType" : NewBodyOperationType.REMOVE, "oppositeDirection" : true, "depth" : 1 * mm, "offsetDistance" : 25 * mm});
        }
        {
            var Q0;
            Q0=makeQuery(id+"F5.boolean.opBoolean","MERGE",FACE,{"derivedFrom":[makeQuery(id+"F1.opExtrude","CAP_FACE",FACE,{"disambiguationData":[OSD([sQuery(id+"F0.wireOp",EDGE,"E6.bottom"),sQuery(id+"F0.wireOp",EDGE,"E6.left"),sQuery(id+"F0.wireOp",EDGE,"E6.right"),sQuery(id+"F0.wireOp",EDGE,"E12.MirrorCS"),sQuery(id+"F0.wireOp",EDGE,"E13.MirrorCS"),sQuery(id+"F0.wireOp",EDGE,"E14.MirrorCS"),sQuery(id+"F0.wireOp",EDGE,"E16"),sQuery(id+"F0.wireOp",EDGE,"E17")])],"isStart":true}),makeQuery(id+"F5.opExtrude","SWEPT_FACE",FACE,{"disambiguationData":[OSD([sQuery(id+"F4.wireOp",EDGE,"E33.top")])]}),makeQuery(id+"F5.opExtrude","SWEPT_FACE",FACE,{"disambiguationData":[OSD([sQuery(id+"F4.wireOp",EDGE,"E35.MirrorCS")])]})]});
            var sketch = newSketch(context, id + "F32", { "sketchPlane" : qUnion([Q0])});
            skLineSegment(sketch, "E124", {"start": v(22.5, 10.5) * mm, "end": v(22.5, -5.66) * mm});
            skLineSegment(sketch, "E125", {"start": v(22.5, -5.66) * mm, "end": v(25.5, -5.66) * mm});
            skLineSegment(sketch, "E126", {"start": v(25.5, -5.66) * mm, "end": v(25.5, 10.5) * mm});
            skLineSegment(sketch, "E127", {"start": v(25.5, 10.5) * mm, "end": v(22.5, 10.5) * mm});
            skLineSegment(sketch, "E128", {"start": v(22.5, -10.6) * mm, "end": v(22.5, -7.6) * mm});
            skLineSegment(sketch, "E129", {"start": v(22.5, -7.6) * mm, "end": v(25.6, -7.6) * mm});
            skLineSegment(sketch, "E130", {"start": v(25.6, -7.6) * mm, "end": v(25.6, 10.5) * mm});
            skLineSegment(sketch, "E131", {"start": v(25.6, 10.5) * mm, "end": v(28.6, 10.5) * mm});
            skLineSegment(sketch, "E132", {"start": v(28.6, 10.5) * mm, "end": v(28.6, -10.6) * mm});
            skLineSegment(sketch, "E133", {"start": v(28.6, -10.6) * mm, "end": v(22.5, -10.6) * mm});
            skLineSegment(sketch, "E134.0", {"start": v(-25.5, -10.5) * mm, "end": v(-22.5, -10.5) * mm});
            skLineSegment(sketch, "E135.0", {"start": v(-25.5, 10.5) * mm, "end": v(-22.5, 10.5) * mm});
            skLineSegment(sketch, "E136", {"start": v(-25.5, -10.5) * mm, "end": v(-25.5, 6.72) * mm});
            skLineSegment(sketch, "E137", {"start": v(-25.5, 6.72) * mm, "end": v(-22.5, 6.72) * mm});
            skLineSegment(sketch, "E138", {"start": v(-22.5, 6.72) * mm, "end": v(-22.5, -10.5) * mm});
            skLineSegment(sketch, "E139", {"start": v(-22.5, 10.5) * mm, "end": v(-22.4, 10.5) * mm});
            skLineSegment(sketch, "E140", {"start": v(-22.4, 10.5) * mm, "end": v(-22.4, -10.27) * mm});
            skLineSegment(sketch, "E141", {"start": v(-22.4, -10.27) * mm, "end": v(-19.4, -10.27) * mm});
            skLineSegment(sketch, "E142", {"start": v(-19.4, -10.27) * mm, "end": v(-19.4, 13.69) * mm});
            skLineSegment(sketch, "E143", {"start": v(-19.4, 13.69) * mm, "end": v(-22.5, 13.69) * mm});
            skLineSegment(sketch, "E144", {"start": v(-22.5, 13.69) * mm, "end": v(-22.5, 10.5) * mm});
            skSolve(sketch);
        }
        {
            var Q0;
            Q0 = qSketchRegion(id + "F32", true);
            var Q1;
            {var subQ0=sQuery(id+"F0.wireOp",EDGE,"E14.MirrorCS");var subQ1=sQuery(id+"F0.wireOp",EDGE,"E6.right");var subQ2=sQuery(id+"F0.wireOp",EDGE,"E17");var subQ3=sQuery(id+"F0.wireOp",EDGE,"E6.bottom");Q1=makeQuery(id+"F3.boolean.opBoolean","SPLIT",FACE,{"disambiguationData":[TD([makeQuery(id+"F1.opExtrude","SWEPT_FACE",FACE,{"disambiguationData":[OSD([subQ1])]})])],"derivedFrom":makeQuery(id+"F1.opExtrude","CAP_FACE",FACE,{"disambiguationData":[OSD([subQ3,sQuery(id+"F0.wireOp",EDGE,"E6.left"),subQ1,sQuery(id+"F0.wireOp",EDGE,"E12.MirrorCS"),sQuery(id+"F0.wireOp",EDGE,"E13.MirrorCS"),subQ0,sQuery(id+"F0.wireOp",EDGE,"E16"),subQ2])],"isStart":false})});}
            extrude(context, id + "F33", {"entities" : qUnion([Q0]), "operationType" : NewBodyOperationType.ADD, "endBound" : BoundingType.UP_TO_SURFACE, "oppositeDirection" : true, "depth" : 25 * mm, "endBoundEntityFace" : qUnion([Q1]), "offsetDistance" : 25 * mm});
        }
        {
            var Q0;
            Q0=makeQuery(id+"F33.boolean.opBoolean","MERGE",FACE,{"derivedFrom":[makeQuery(id+"F1.opExtrude","SWEPT_FACE",FACE,{"disambiguationData":[OSD([sQuery(id+"F0.wireOp",EDGE,"E8")])]}),makeQuery(id+"F33.opExtrude","SWEPT_FACE",FACE,{"disambiguationData":[OSD([sQuery(id+"F32.wireOp",EDGE,"E136")])]})]});
            var sketch = newSketch(context, id + "F34", { "sketchPlane" : qUnion([Q0])});
            skLineSegment(sketch, "E145", {"start": v(3.36, 4) * mm, "end": v(-2.1, 4) * mm, "construction": true});
            skPoint(sketch, "E145.startSnap0", {"position": v(6.72, 4) * mm});
            skArc(sketch, "E146.0.startCap", {"start": v(3.36, 5.65) * mm, "mid": v(5, 4) * mm, "end": v(3.36, 2.35) * mm});
            skArc(sketch, "E146.0.endCap", {"start": v(-2.1, 2.35) * mm, "mid": v(-3.74, 4) * mm, "end": v(-2.1, 5.65) * mm});
            skLineSegment(sketch, "E146.0.left", {"start": v(3.36, 2.35) * mm, "end": v(-2.1, 2.35) * mm});
            skLineSegment(sketch, "E146.0.right", {"start": v(3.36, 5.65) * mm, "end": v(-2.1, 5.65) * mm});
            skSolve(sketch);
        }
        {
            var Q0;
            Q0 = qSketchRegion(id + "F34", true);
            extrude(context, id + "F35", {"entities" : qUnion([Q0]), "operationType" : NewBodyOperationType.REMOVE, "endBound" : BoundingType.THROUGH_ALL, "oppositeDirection" : true, "depth" : 25 * mm, "offsetDistance" : 25 * mm});
        }
        {
            var Q0;
            Q0=qCreatedBy(makeId("Top.planeOp"),FACE);
            var sketch = newSketch(context, id + "F36", { "sketchPlane" : qUnion([Q0])});
            skLineSegment(sketch, "E147", {"start": v(-6.2, 0) * mm, "end": v(-6.2, 5) * mm});
            skLineSegment(sketch, "E148", {"start": v(-6.2, 5) * mm, "end": v(1.8, 5) * mm});
            skLineSegment(sketch, "E149", {"start": v(1.8, 5) * mm, "end": v(1.8, 4) * mm});
            skLineSegment(sketch, "E150", {"start": v(1.8, 4) * mm, "end": v(17.1, 4) * mm});
            skLineSegment(sketch, "E151", {"start": v(17.1, 4) * mm, "end": v(17.1, 0) * mm});
            skLineSegment(sketch, "E152.MirrorCS", {"start": v(1.8, -5) * mm, "end": v(1.8, -4) * mm});
            skLineSegment(sketch, "E153.MirrorCS", {"start": v(17.1, -4) * mm, "end": v(17.1, 0) * mm});
            skLineSegment(sketch, "E154.MirrorCS", {"start": v(-6.2, -5) * mm, "end": v(1.8, -5) * mm});
            skLineSegment(sketch, "E155.MirrorCS", {"start": v(1.8, -4) * mm, "end": v(17.1, -4) * mm});
            skLineSegment(sketch, "E156.MirrorCS", {"start": v(-6.2, 0) * mm, "end": v(-6.2, -5) * mm});
            skLineSegment(sketch, "E157", {"start": v(12.45, 0) * mm, "end": v(6.45, 0) * mm});
            skArc(sketch, "E158.0.startCap", {"start": v(12.45, 1.65) * mm, "mid": v(14.1, 0) * mm, "end": v(12.45, -1.65) * mm});
            skArc(sketch, "E158.0.endCap", {"start": v(6.45, -1.65) * mm, "mid": v(4.8, 0) * mm, "end": v(6.45, 1.65) * mm});
            skLineSegment(sketch, "E158.0.left", {"start": v(12.45, -1.65) * mm, "end": v(6.45, -1.65) * mm});
            skLineSegment(sketch, "E158.0.right", {"start": v(12.45, 1.65) * mm, "end": v(6.45, 1.65) * mm});
            skLineSegment(sketch, "E159.bottom", {"start": v(-0.2, -3) * mm, "end": v(-4.2, -3) * mm});
            skLineSegment(sketch, "E159.top", {"start": v(-0.2, 3) * mm, "end": v(-4.2, 3) * mm});
            skLineSegment(sketch, "E159.left", {"start": v(-0.2, -3) * mm, "end": v(-0.2, 3) * mm});
            skLineSegment(sketch, "E159.right", {"start": v(-4.2, -3) * mm, "end": v(-4.2, 3) * mm});
            skPoint(sketch, "E159.middle", {"position": v(-2.2, 0) * mm});
            skSolve(sketch);
        }
        {
            var Q0;
            Q0 = qSketchRegion(id + "F36", true);
            extrude(context, id + "F37", {"entities" : qUnion([Q0]), "depth" : 3 * mm, "offsetDistance" : 25 * mm});
        }
        {
            var Q0;
            Q0=makeQuery(id+"F37.opExtrude","CAP_EDGE",EDGE,{"disambiguationData":[OSD([sQuery(id+"F36.wireOp",EDGE,"E159.top")])],"isStart":false});
            var Q1;
            Q1=makeQuery(id+"F37.opExtrude","CAP_EDGE",EDGE,{"disambiguationData":[OSD([sQuery(id+"F36.wireOp",EDGE,"E159.top")])],"isStart":true});
            var Q2;
            Q2=makeQuery(id+"F37.opExtrude","CAP_EDGE",EDGE,{"disambiguationData":[OSD([sQuery(id+"F36.wireOp",EDGE,"E159.bottom")])],"isStart":false});
            var Q3;
            Q3=makeQuery(id+"F37.opExtrude","CAP_EDGE",EDGE,{"disambiguationData":[OSD([sQuery(id+"F36.wireOp",EDGE,"E159.bottom")])],"isStart":true});
            var Q4;
            Q4=makeQuery(id+"F37.opExtrude","CAP_EDGE",EDGE,{"disambiguationData":[OSD([sQuery(id+"F36.wireOp",EDGE,"E159.right")])],"isStart":false});
            var Q5;
            Q5=makeQuery(id+"F37.opExtrude","CAP_EDGE",EDGE,{"disambiguationData":[OSD([sQuery(id+"F36.wireOp",EDGE,"E159.left")])],"isStart":false});
            var Q6;
            Q6=makeQuery(id+"F37.opExtrude","CAP_EDGE",EDGE,{"disambiguationData":[OSD([sQuery(id+"F36.wireOp",EDGE,"E159.left")])],"isStart":true});
            var Q7;
            Q7=makeQuery(id+"F37.opExtrude","CAP_EDGE",EDGE,{"disambiguationData":[OSD([sQuery(id+"F36.wireOp",EDGE,"E159.right")])],"isStart":true});
            fillet(context, id + "F38", {"entities" : qUnion([Q0, Q1, Q2, Q3, Q4, Q5, Q6, Q7]), "radius" : 1.5 * mm, "tangentPropagation" : true, "allowEdgeOverflow" : false});
        }
        {
            var Q0;
            Q0=makeQuery(id+"F37.opExtrude","SWEPT_EDGE",EDGE,{"disambiguationData":[OSD([sQuery(id+"F36.wireOp",EDGE,"E150"),sQuery(id+"F36.wireOp",EDGE,"E151")])]});
            var Q1;
            Q1=makeQuery(id+"F37.opExtrude","SWEPT_EDGE",EDGE,{"disambiguationData":[OSD([sQuery(id+"F36.wireOp",EDGE,"E153.MirrorCS"),sQuery(id+"F36.wireOp",EDGE,"E155.MirrorCS")])]});
            fillet(context, id + "F39", {"entities" : qUnion([Q0, Q1]), "radius" : 4 * mm, "tangentPropagation" : true, "allowEdgeOverflow" : false});
        }
    });
